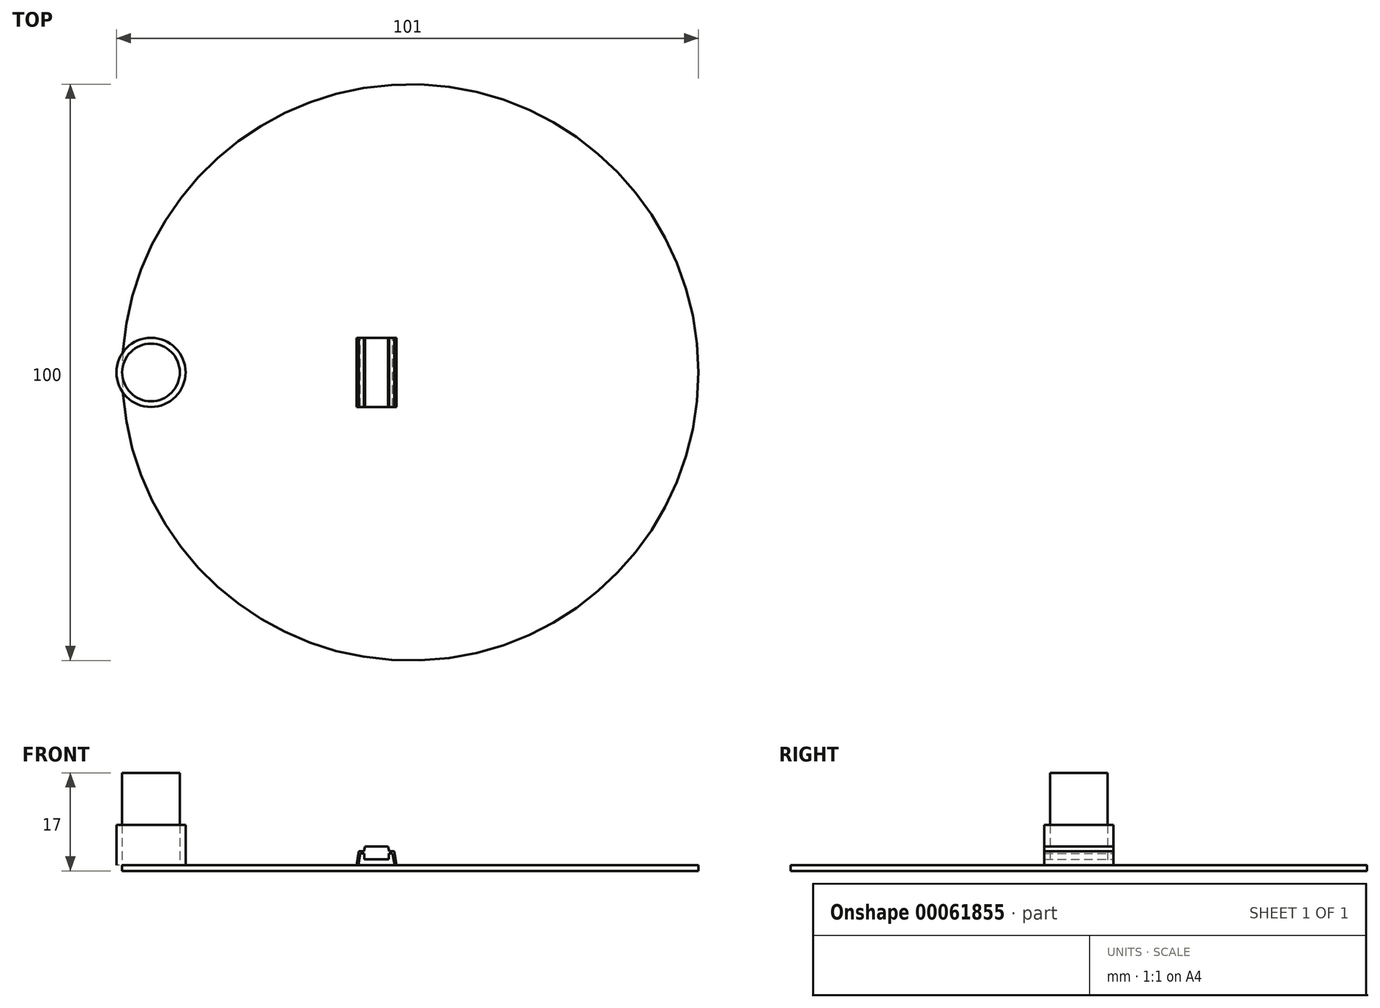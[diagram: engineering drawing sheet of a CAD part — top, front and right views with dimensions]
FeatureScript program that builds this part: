
annotation { "Feature Type Name" : "Feature", "Feature Type Description" : "" }
export const myFeature = defineFeature(function(context is Context, id is Id, definition is map)
    precondition{}
    {
        {
            var Q0;
            Q0=qCreatedBy(makeId("Top.planeOp"),FACE);
            var sketch = newSketch(context, id + "F0", { "sketchPlane" : qUnion([Q0])});
            skCircle(sketch, "E0", {"center": v(0, 0) * mm, "radius": 50 * mm});
            skSolve(sketch);
        }
        {
            var Q0;
            Q0 = qSketchRegion(id + "F0", true);
            extrude(context, id + "F1", {"entities" : qUnion([Q0]), "oppositeDirection" : true, "depth" : 1 * mm});
        }
        {
            var Q0;
            Q0=qCreatedBy(makeId("Top.planeOp"),FACE);
            var sketch = newSketch(context, id + "F2", { "sketchPlane" : qUnion([Q0])});
            skCircle(sketch, "E1", {"center": v(-45, 0) * mm, "radius": 5 * mm});
            skSolve(sketch);
        }
        {
            var Q0;
            Q0 = qSketchRegion(id + "F2", true);
            extrude(context, id + "F3", {"entities" : qUnion([Q0]), "depth" : 16 * mm});
        }
        {
            var Q0;
            Q0=qCreatedBy(makeId("Front.planeOp"),FACE);
            var sketch = newSketch(context, id + "F4", { "sketchPlane" : qUnion([Q0])});
            skLineSegment(sketch, "E2", {"start": v(-9.33, 0) * mm, "end": v(-8.95, 2.42) * mm});
            skLineSegment(sketch, "E3", {"start": v(-8.95, 2.42) * mm, "end": v(-8.05, 2.42) * mm});
            skLineSegment(sketch, "E4", {"start": v(-8.05, 2.42) * mm, "end": v(-7.87, 3.2) * mm});
            skLineSegment(sketch, "E5", {"start": v(-7.87, 3.2) * mm, "end": v(-5.87, 3.2) * mm});
            skLineSegment(sketch, "E6", {"start": v(-5.87, 3.2) * mm, "end": v(-5.87, 1) * mm});
            skLineSegment(sketch, "E7", {"start": v(-5.87, 1) * mm, "end": v(-8, 1) * mm});
            skLineSegment(sketch, "E8", {"start": v(-8, 1) * mm, "end": v(-8, 2.02) * mm});
            skLineSegment(sketch, "E9", {"start": v(-8, 2.02) * mm, "end": v(-8.67, 2.02) * mm});
            skLineSegment(sketch, "E10", {"start": v(-8.67, 2.02) * mm, "end": v(-9.01, 0) * mm});
            skLineSegment(sketch, "E11", {"start": v(-9.01, 0) * mm, "end": v(-9.33, 0) * mm});
            skSolve(sketch);
        }
        {
            var Q0;
            Q0 = qSketchRegion(id + "F4", true);
            extrude(context, id + "F5", {"entities" : qUnion([Q0]), "endBound" : BoundingType.SYMMETRIC, "depth" : 12 * mm});
        }
        {
            var Q0;
            Q0=makeQuery(id+"F5.opExtrude","SWEPT_BODY",BODY,{"disambiguationData":[OSD([sQuery(id+"F4.wireOp",EDGE,"E2"),sQuery(id+"F4.wireOp",EDGE,"E3"),sQuery(id+"F4.wireOp",EDGE,"E4"),sQuery(id+"F4.wireOp",EDGE,"E5"),sQuery(id+"F4.wireOp",EDGE,"E6"),sQuery(id+"F4.wireOp",EDGE,"E7"),sQuery(id+"F4.wireOp",EDGE,"E8"),sQuery(id+"F4.wireOp",EDGE,"E9"),sQuery(id+"F4.wireOp",EDGE,"E10"),sQuery(id+"F4.wireOp",EDGE,"E11")])]});
            var Q1;
            Q1=makeQuery(id+"F5.opExtrude","SWEPT_FACE",FACE,{"disambiguationData":[OSD([sQuery(id+"F4.wireOp",EDGE,"E6")])]});
            mirror(context, id + "F6", {"operationType" : NewBodyOperationType.ADD, "entities" : qUnion([Q0]), "mirrorPlane" : qUnion([Q1])});
        }
        {
            var Q0;
            Q0=qCreatedBy(makeId("Top.planeOp"),FACE);
            var sketch = newSketch(context, id + "F7", { "sketchPlane" : qUnion([Q0])});
            skLineSegment(sketch, "E12.rect.bottom", {"start": v(31.82, -31.82) * mm, "end": v(-31.82, -31.82) * mm, "construction": true});
            skLineSegment(sketch, "E12.rect.top", {"start": v(31.82, 31.82) * mm, "end": v(-31.82, 31.82) * mm, "construction": true});
            skLineSegment(sketch, "E12.rect.left", {"start": v(31.82, -31.82) * mm, "end": v(31.82, 31.82) * mm, "construction": true});
            skLineSegment(sketch, "E12.rect.right", {"start": v(-31.82, -31.82) * mm, "end": v(-31.82, 31.82) * mm, "construction": true});
            skPoint(sketch, "E12.rect.middle", {"position": v(0, 0) * mm});
            skLineSegment(sketch, "E13", {"start": v(31.82, 31.82) * mm, "end": v(35.36, 35.36) * mm, "construction": true});
            skLineSegment(sketch, "E14", {"start": v(0, 0) * mm, "end": v(-31.82, 0) * mm, "construction": true});
            skPoint(sketch, "E15", {"position": v(-15.9, 0) * mm});
            skSolve(sketch);
        }
        {
            var Q0;
            Q0=qCreatedBy(makeId("Top.planeOp"),FACE);
            var sketch = newSketch(context, id + "F8", { "sketchPlane" : qUnion([Q0])});
            skCircle(sketch, "E16", {"center": v(-45, 0) * mm, "radius": 6 * mm});
            skSolve(sketch);
        }
        {
            var Q0;
            Q0 = qSketchRegion(id + "F8", true);
            extrude(context, id + "F9", {"entities" : qUnion([Q0]), "depth" : 7 * mm});
        }
    });
